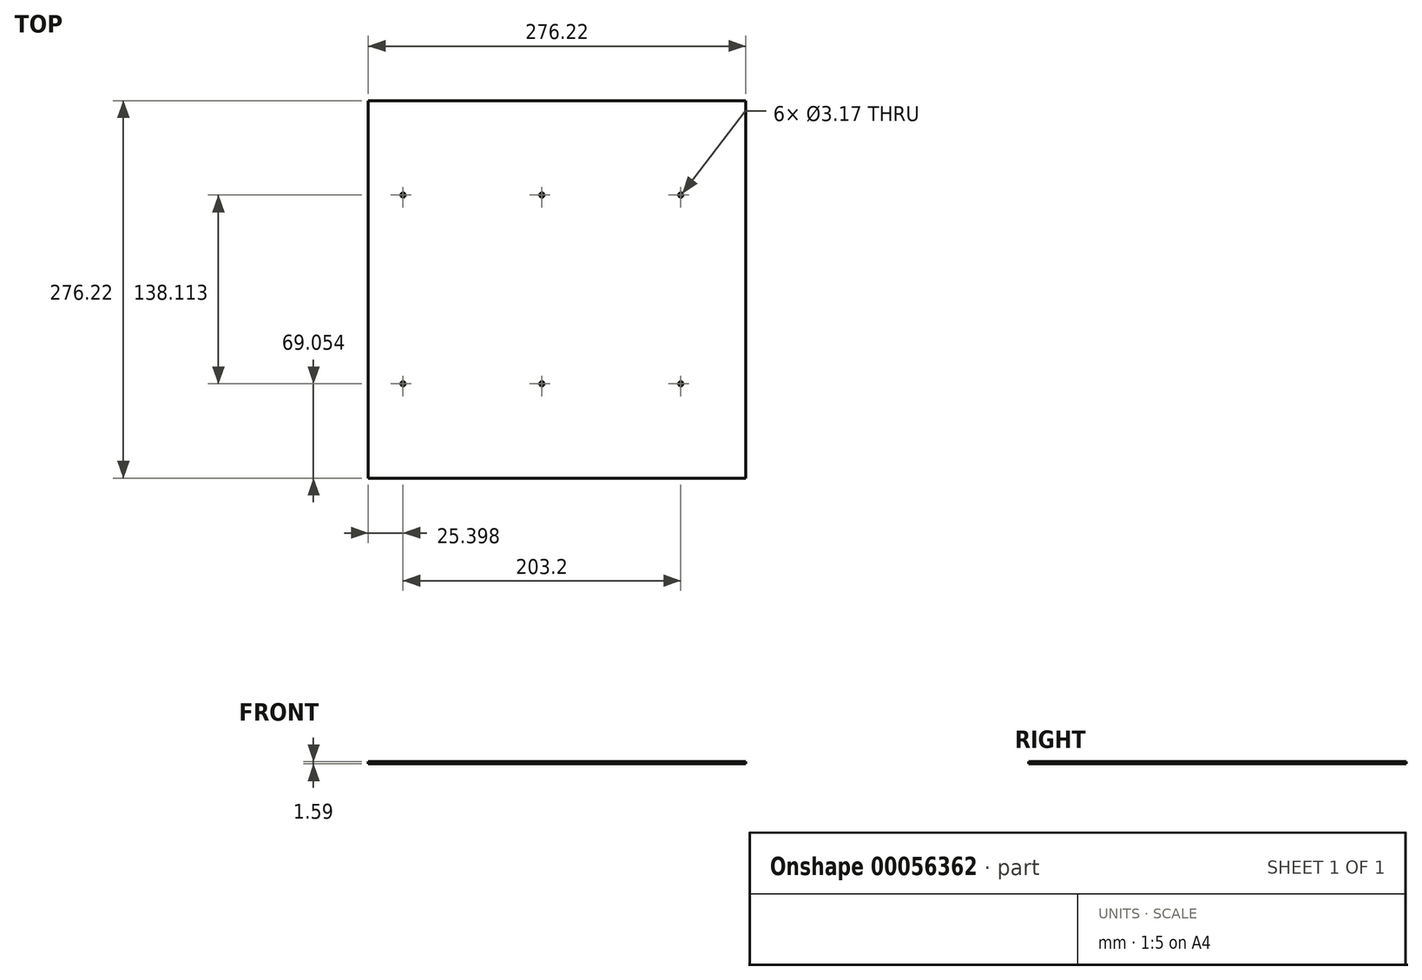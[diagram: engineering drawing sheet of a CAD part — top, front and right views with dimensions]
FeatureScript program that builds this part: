
annotation { "Feature Type Name" : "Feature", "Feature Type Description" : "" }
export const myFeature = defineFeature(function(context is Context, id is Id, definition is map)
    precondition{}
    {
        {
            var Q0;
            Q0=qCreatedBy(makeId("Top.planeOp"),FACE);
            var sketch = newSketch(context, id + "F0", { "sketchPlane" : qUnion([Q0])});
            skLineSegment(sketch, "E0.rect.bottom", {"start": v(-138.11, 138.11) * mm, "end": v(138.11, 138.11) * mm});
            skLineSegment(sketch, "E0.rect.top", {"start": v(-138.11, -138.11) * mm, "end": v(138.11, -138.11) * mm});
            skLineSegment(sketch, "E0.rect.left", {"start": v(-138.11, 138.11) * mm, "end": v(-138.11, -138.11) * mm});
            skLineSegment(sketch, "E0.rect.right", {"start": v(138.11, 138.11) * mm, "end": v(138.11, -138.11) * mm});
            skPoint(sketch, "E0.rect.middle", {"position": v(0, 0) * mm});
            skSolve(sketch);
        }
        {
            var Q0;
            Q0=makeQuery(id+"F0.imprint","IMPRINT",FACE,{"disambiguationData":[TD([[makeQuery(id+"F0.imprint","IMPRINT",EDGE,{"derivedFrom":sQuery(id+"F0.wireOp",EDGE,"E0.rect.bottom")}),-1.0]])]});
            var sketch = newSketch(context, id + "F1", { "sketchPlane" : qUnion([Q0])});
            skLineSegment(sketch, "E1", {"start": v(138.47, 0) * mm, "end": v(-137.87, 0) * mm, "construction": true});
            skLineSegment(sketch, "E2", {"start": v(-138.11, 69.06) * mm, "end": v(138.23, 69.06) * mm, "construction": true});
            skLineSegment(sketch, "E3.0", {"start": v(-138.11, 138.11) * mm, "end": v(-138.11, 0) * mm, "construction": true});
            skLineSegment(sketch, "E4", {"start": v(-138.11, 0) * mm, "end": v(-138.11, -138.11) * mm, "construction": true});
            skLineSegment(sketch, "E5", {"start": v(-138.11, -69.06) * mm, "end": v(138.23, -69.06) * mm, "construction": true});
            skLineSegment(sketch, "E6.0", {"start": v(-112.71, 138.11) * mm, "end": v(-112.71, -138.11) * mm, "construction": true});
            skLineSegment(sketch, "E7.0", {"start": v(-11.11, 138.11) * mm, "end": v(-11.11, -138.11) * mm, "construction": true});
            skLineSegment(sketch, "E8.0", {"start": v(90.49, 138.11) * mm, "end": v(90.49, -138.11) * mm, "construction": true});
            skPoint(sketch, "E9", {"position": v(-112.71, -69.06) * mm});
            skPoint(sketch, "E10", {"position": v(-11.11, -69.06) * mm});
            skPoint(sketch, "E11", {"position": v(90.49, -69.06) * mm});
            skPoint(sketch, "E12", {"position": v(-112.71, 69.06) * mm});
            skPoint(sketch, "E13", {"position": v(-11.11, 69.06) * mm});
            skPoint(sketch, "E14", {"position": v(90.49, 69.06) * mm});
            skCircle(sketch, "E15", {"center": v(-112.71, 69.06) * mm, "radius": 1.59 * mm});
            skCircle(sketch, "E16", {"center": v(-11.11, 69.06) * mm, "radius": 1.59 * mm});
            skCircle(sketch, "E17", {"center": v(90.49, 69.06) * mm, "radius": 1.59 * mm});
            skCircle(sketch, "E18", {"center": v(-112.71, -69.06) * mm, "radius": 1.59 * mm});
            skCircle(sketch, "E19", {"center": v(-11.11, -69.06) * mm, "radius": 1.59 * mm});
            skCircle(sketch, "E20", {"center": v(90.49, -69.06) * mm, "radius": 1.59 * mm});
            skSolve(sketch);
        }
        {
            var Q0;
            Q0 = qSketchRegion(id + "F0", true);
            var Q1;
            Q1=makeQuery(id+"F0.imprint","IMPRINT",FACE,{"disambiguationData":[TD([[makeQuery(id+"F0.imprint","IMPRINT",EDGE,{"derivedFrom":sQuery(id+"F0.wireOp",EDGE,"E0.rect.bottom")}),-1.0]])]});
            extrude(context, id + "F2", {"entities" : qUnion([Q0, Q1]), "oppositeDirection" : true, "depth" : 1.59 * mm});
        }
        {
            var Q0;
            Q0=makeQuery(id+"F1.imprint","IMPRINT",FACE,{"disambiguationData":[TD([[makeQuery(id+"F1.imprint","IMPRINT",EDGE,{"derivedFrom":sQuery(id+"F1.wireOp",EDGE,"E17")}),1.0]])]});
            var Q1;
            Q1=makeQuery(id+"F1.imprint","IMPRINT",FACE,{"disambiguationData":[TD([[makeQuery(id+"F1.imprint","IMPRINT",EDGE,{"derivedFrom":sQuery(id+"F1.wireOp",EDGE,"E16")}),1.0]])]});
            var Q2;
            Q2=makeQuery(id+"F1.imprint","IMPRINT",FACE,{"disambiguationData":[TD([[makeQuery(id+"F1.imprint","IMPRINT",EDGE,{"derivedFrom":sQuery(id+"F1.wireOp",EDGE,"E15")}),1.0]])]});
            var Q3;
            Q3=makeQuery(id+"F1.imprint","IMPRINT",FACE,{"disambiguationData":[TD([[makeQuery(id+"F1.imprint","IMPRINT",EDGE,{"derivedFrom":sQuery(id+"F1.wireOp",EDGE,"E18")}),1.0]])]});
            var Q4;
            Q4=makeQuery(id+"F1.imprint","IMPRINT",FACE,{"disambiguationData":[TD([[makeQuery(id+"F1.imprint","IMPRINT",EDGE,{"derivedFrom":sQuery(id+"F1.wireOp",EDGE,"E19")}),1.0]])]});
            var Q5;
            Q5=makeQuery(id+"F1.imprint","IMPRINT",FACE,{"disambiguationData":[TD([[makeQuery(id+"F1.imprint","IMPRINT",EDGE,{"derivedFrom":sQuery(id+"F1.wireOp",EDGE,"E20")}),1.0]])]});
            extrude(context, id + "F3", {"entities" : qUnion([Q0, Q1, Q2, Q3, Q4, Q5]), "operationType" : NewBodyOperationType.REMOVE, "endBound" : BoundingType.UP_TO_NEXT, "oppositeDirection" : true, "depth" : 25.4 * mm});
        }
    });
